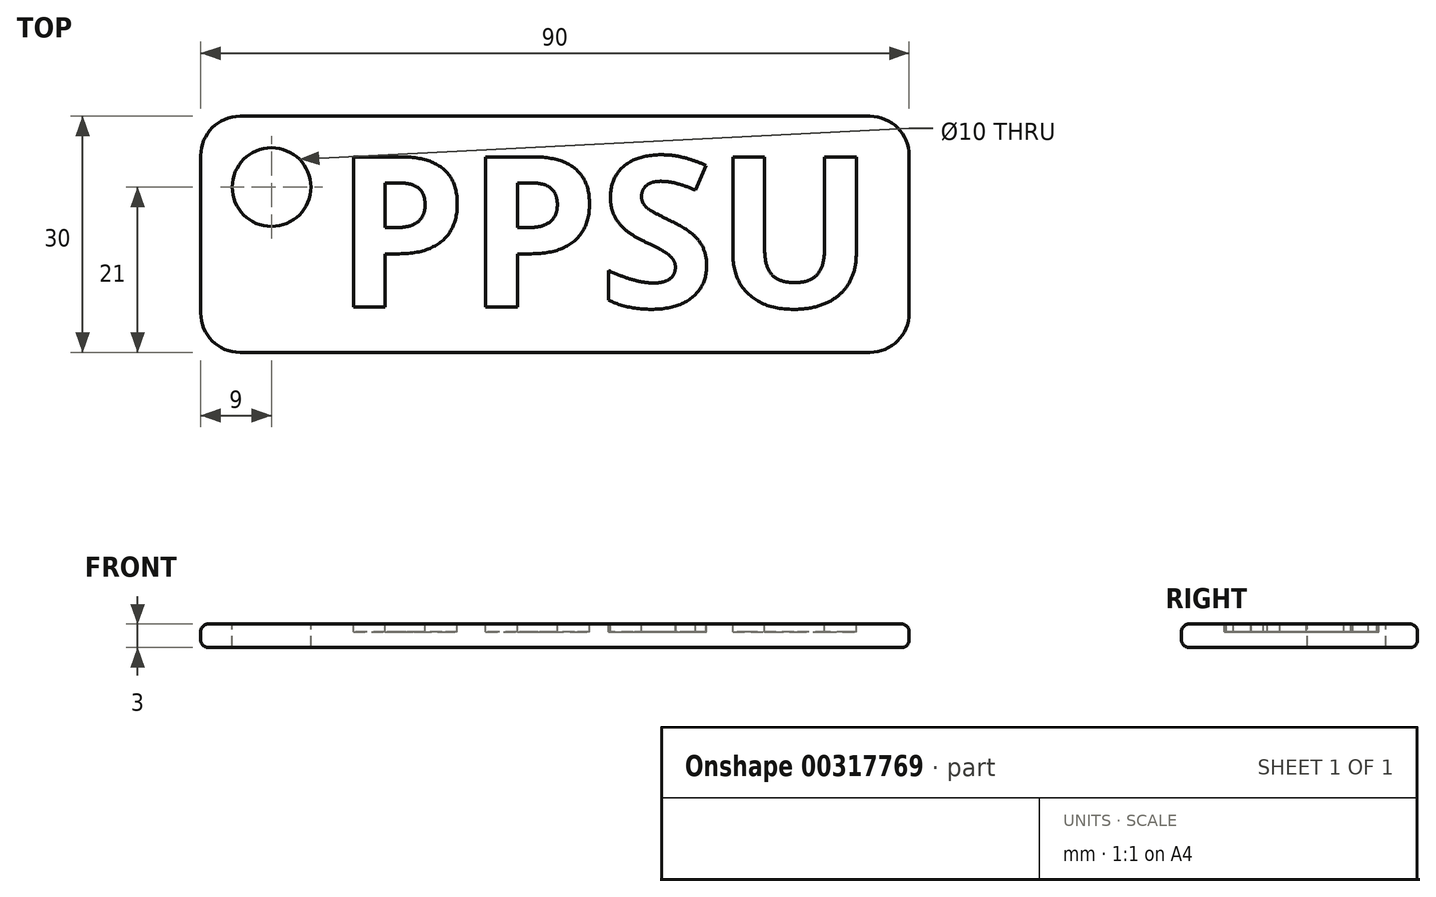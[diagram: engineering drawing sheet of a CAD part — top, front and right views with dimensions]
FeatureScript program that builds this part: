
annotation { "Feature Type Name" : "Feature", "Feature Type Description" : "" }
export const myFeature = defineFeature(function(context is Context, id is Id, definition is map)
    precondition{}
    {
        {
            var Q0;
            Q0=qCreatedBy(makeId("Top.planeOp"),FACE);
            var sketch = newSketch(context, id + "F0", { "sketchPlane" : qUnion([Q0])});
            skLineSegment(sketch, "E0.bottom", {"start": v(-45, 15) * mm, "end": v(45, 15) * mm});
            skLineSegment(sketch, "E0.top", {"start": v(-45, -15) * mm, "end": v(45, -15) * mm});
            skLineSegment(sketch, "E0.left", {"start": v(-45, 15) * mm, "end": v(-45, -15) * mm});
            skLineSegment(sketch, "E0.right", {"start": v(45, 15) * mm, "end": v(45, -15) * mm});
            skLineSegment(sketch, "E1", {"start": v(-45, 15) * mm, "end": v(45, -15) * mm, "construction": true});
            skSolve(sketch);
        }
        {
            var Q0;
            Q0=makeQuery(id+"F0.imprint","IMPRINT",FACE,{"disambiguationData":[TD([[makeQuery(id+"F0.imprint","IMPRINT",EDGE,{"derivedFrom":sQuery(id+"F0.wireOp",EDGE,"E0.bottom")}),-1.0]])]});
            extrude(context, id + "F1", {"entities" : qUnion([Q0]), "depth" : 3 * mm});
        }
        {
            var Q0;
            Q0=makeQuery(id+"F1.opExtrude","CAP_FACE",FACE,{"disambiguationData":[OSD([sQuery(id+"F0.wireOp",EDGE,"E0.bottom"),sQuery(id+"F0.wireOp",EDGE,"E0.top"),sQuery(id+"F0.wireOp",EDGE,"E0.left"),sQuery(id+"F0.wireOp",EDGE,"E0.right")])],"isStart":false});
            var Q1;
            Q1=makeQuery(id+"F1.opExtrude","CAP_FACE",FACE,{"disambiguationData":[OSD([sQuery(id+"F0.wireOp",EDGE,"E0.bottom"),sQuery(id+"F0.wireOp",EDGE,"E0.top"),sQuery(id+"F0.wireOp",EDGE,"E0.left"),sQuery(id+"F0.wireOp",EDGE,"E0.right")])],"isStart":true});
            fillet(context, id + "F2", {"entities" : qUnion([Q0, Q1]), "radius" : 1 * mm, "tangentPropagation" : true, "allowEdgeOverflow" : false});
        }
        {
            var Q0;
            Q0=makeQuery(id+"F1.opExtrude","SWEPT_EDGE",EDGE,{"disambiguationData":[OSD([sQuery(id+"F0.wireOp",EDGE,"E0.top"),sQuery(id+"F0.wireOp",EDGE,"E0.right")])]});
            var Q1;
            Q1=makeQuery(id+"F1.opExtrude","SWEPT_EDGE",EDGE,{"disambiguationData":[OSD([sQuery(id+"F0.wireOp",EDGE,"E0.bottom"),sQuery(id+"F0.wireOp",EDGE,"E0.right")])]});
            var Q2;
            Q2=makeQuery(id+"F1.opExtrude","SWEPT_EDGE",EDGE,{"disambiguationData":[OSD([sQuery(id+"F0.wireOp",EDGE,"E0.bottom"),sQuery(id+"F0.wireOp",EDGE,"E0.left")])]});
            var Q3;
            Q3=makeQuery(id+"F1.opExtrude","SWEPT_EDGE",EDGE,{"disambiguationData":[OSD([sQuery(id+"F0.wireOp",EDGE,"E0.top"),sQuery(id+"F0.wireOp",EDGE,"E0.left")])]});
            fillet(context, id + "F3", {"entities" : qUnion([Q0, Q1, Q2, Q3]), "radius" : 5 * mm, "tangentPropagation" : true, "allowEdgeOverflow" : false});
        }
        {
            var Q0;
            {var subQ0=sQuery(id+"F0.wireOp",EDGE,"E0.left");var subQ2=sQuery(id+"F0.wireOp",EDGE,"E0.bottom");var subQ4=sQuery(id+"F0.wireOp",EDGE,"E0.right");var subQ6=sQuery(id+"F0.wireOp",EDGE,"E0.top");Q0=makeQuery(id+"FmQCBBX3Ub0qneL_1.boolean.opBoolean","SPLIT",FACE,{"disambiguationData":[TD([makeQuery(id+"FmQCBBX3Ub0qneL_1.opExtrude","SWEPT_FACE",FACE,{"disambiguationData":[OSD([sQuery(id+"FOCoeRmDbjhRCuz_1.wireOp",EDGE,"4a1fb44a-e7be-4e23-9449-000d953c446c.sketch_text.stroke-0")])]})])],"derivedFrom":makeQuery(id+"F1.opExtrude","CAP_FACE",FACE,{"disambiguationData":[OSD([subQ2,subQ6,subQ0,subQ4])],"isStart":false})});}
            var sketch = newSketch(context, id + "F4", { "sketchPlane" : qUnion([Q0])});
            skCircle(sketch, "E2", {"center": v(-36, 6) * mm, "radius": 5 * mm});
            skSolve(sketch);
        }
        {
            var Q0;
            Q0=qSketchRegion(id+"F4",true);
            extrude(context, id + "F5", {"entities" : qUnion([Q0]), "operationType" : NewBodyOperationType.REMOVE, "oppositeDirection" : true, "depth" : 3 * mm});
        }
        {
            var Q0;
            Q0=makeQuery(id+"F1.opExtrude","CAP_FACE",FACE,{"disambiguationData":[OSD([sQuery(id+"F0.wireOp",EDGE,"E0.bottom"),sQuery(id+"F0.wireOp",EDGE,"E0.top"),sQuery(id+"F0.wireOp",EDGE,"E0.left"),sQuery(id+"F0.wireOp",EDGE,"E0.right")])],"isStart":false});
            var sketch = newSketch(context, id + "F6", { "sketchPlane" : qUnion([Q0])});
            skText(sketch, "E3", { "text": "PPSU", "fontName": "OpenSans-Bold.ttf"});
            const initialGuessF6  = {"E3": [-0.028, -0.00926, 1, 0, 0.01926]};
            skSetInitialGuess(sketch, initialGuessF6);
            skSolve(sketch);
        }
        {
            var Q0;
            Q0=qSketchRegion(id+"F6",true);
            extrude(context, id + "F7", {"entities" : qUnion([Q0]), "operationType" : NewBodyOperationType.REMOVE, "oppositeDirection" : true, "depth" : 1 * mm});
        }
    });
